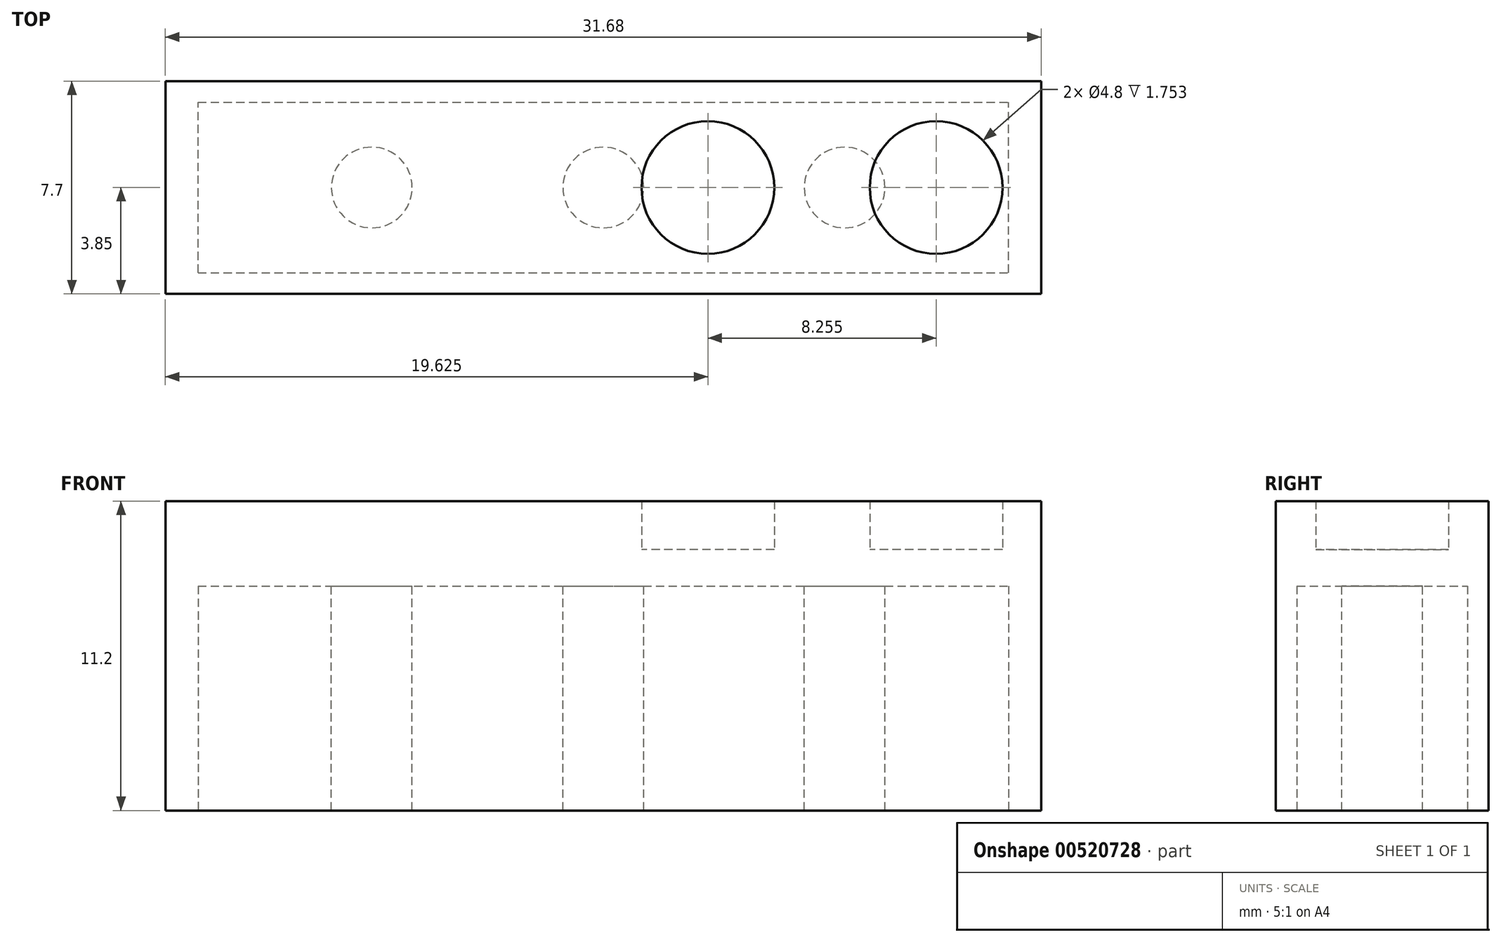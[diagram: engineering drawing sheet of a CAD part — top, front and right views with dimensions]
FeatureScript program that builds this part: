
annotation { "Feature Type Name" : "Feature", "Feature Type Description" : "" }
export const myFeature = defineFeature(function(context is Context, id is Id, definition is map)
    precondition{}
    {
        {
            var Q0;
            Q0=qCreatedBy(makeId("Top.planeOp"),FACE);
            var sketch = newSketch(context, id + "F0", { "sketchPlane" : qUnion([Q0])});
            skLineSegment(sketch, "E0.bottom", {"start": v(-15.84, 3.85) * mm, "end": v(15.84, 3.85) * mm});
            skLineSegment(sketch, "E0.top", {"start": v(-15.84, -3.85) * mm, "end": v(15.84, -3.85) * mm});
            skLineSegment(sketch, "E0.left", {"start": v(-15.84, 3.85) * mm, "end": v(-15.84, -3.85) * mm});
            skLineSegment(sketch, "E0.right", {"start": v(15.84, 3.85) * mm, "end": v(15.84, -3.85) * mm});
            skPoint(sketch, "E0.middle", {"position": v(0, 0) * mm});
            skSolve(sketch);
        }
        {
            var Q0;
            Q0=makeQuery(id+"F0.imprint","IMPRINT",FACE,{"disambiguationData":[TD([[makeQuery(id+"F0.imprint","IMPRINT",EDGE,{"derivedFrom":sQuery(id+"F0.wireOp",EDGE,"E0.bottom")}),-1.0]])]});
            extrude(context, id + "F1", {"entities" : qUnion([Q0]), "depth" : 9.45 * mm, "offsetDistance" : 25.4 * mm});
        }
        {
            var Q0;
            Q0=makeQuery(id+"F1.opExtrude","CAP_FACE",FACE,{"disambiguationData":[OSD([sQuery(id+"F0.wireOp",EDGE,"E0.bottom"),sQuery(id+"F0.wireOp",EDGE,"E0.top"),sQuery(id+"F0.wireOp",EDGE,"E0.left"),sQuery(id+"F0.wireOp",EDGE,"E0.right")])],"isStart":false});
            var sketch = newSketch(context, id + "F2", { "sketchPlane" : qUnion([Q0])});
            skCircle(sketch, "E1", {"center": v(-12.04, 0) * mm, "radius": 2.4 * mm});
            skCircle(sketch, "E2", {"center": v(-3.78, 0) * mm, "radius": 2.4 * mm});
            skCircle(sketch, "E3.MirrorC", {"center": v(3.78, 0) * mm, "radius": 2.4 * mm});
            skCircle(sketch, "E4.MirrorC", {"center": v(12.04, 0) * mm, "radius": 2.4 * mm});
            skSolve(sketch);
        }
        {
            var Q0;
            Q0=makeQuery(id+"F2.imprint","IMPRINT",FACE,{"disambiguationData":[TD([[makeQuery(id+"F2.imprint","IMPRINT",EDGE,{"derivedFrom":sQuery(id+"F2.wireOp",EDGE,"E1")}),1.0]])]});
            var Q1;
            Q1=makeQuery(id+"F2.imprint","IMPRINT",FACE,{"disambiguationData":[TD([[makeQuery(id+"F2.imprint","IMPRINT",EDGE,{"derivedFrom":sQuery(id+"F2.wireOp",EDGE,"E2")}),1.0]])]});
            var Q2;
            Q2=makeQuery(id+"F2.imprint","IMPRINT",FACE,{"disambiguationData":[TD([[makeQuery(id+"F2.imprint","IMPRINT",EDGE,{"derivedFrom":sQuery(id+"F2.wireOp",EDGE,"E3.MirrorC")}),-1.0]])]});
            var Q3;
            Q3=makeQuery(id+"F2.imprint","IMPRINT",FACE,{"disambiguationData":[TD([[makeQuery(id+"F2.imprint","IMPRINT",EDGE,{"derivedFrom":sQuery(id+"F2.wireOp",EDGE,"E4.MirrorC")}),-1.0]])]});
            extrude(context, id + "F3", {"entities" : qUnion([Q0, Q1, Q2, Q3]), "operationType" : NewBodyOperationType.ADD, "depth" : 1.75 * mm, "offsetDistance" : 25.4 * mm});
        }
        {
            var Q0;
            Q0=makeQuery(id+"F1.opExtrude","CAP_FACE",FACE,{"disambiguationData":[OSD([sQuery(id+"F0.wireOp",EDGE,"E0.bottom"),sQuery(id+"F0.wireOp",EDGE,"E0.top"),sQuery(id+"F0.wireOp",EDGE,"E0.left"),sQuery(id+"F0.wireOp",EDGE,"E0.right")])],"isStart":true});
            var sketch = newSketch(context, id + "F4", { "sketchPlane" : qUnion([Q0])});
            skLineSegment(sketch, "E5.bottom", {"start": v(-14.66, 3.09) * mm, "end": v(14.66, 3.09) * mm});
            skLineSegment(sketch, "E5.top", {"start": v(-14.66, -3.09) * mm, "end": v(14.66, -3.09) * mm});
            skLineSegment(sketch, "E5.left", {"start": v(-14.66, 3.09) * mm, "end": v(-14.66, -3.09) * mm});
            skLineSegment(sketch, "E5.right", {"start": v(14.66, 3.09) * mm, "end": v(14.66, -3.09) * mm});
            skPoint(sketch, "E5.middle", {"position": v(0, 0) * mm});
            skSolve(sketch);
        }
        {
            var Q0;
            Q0=makeQuery(id+"F4.imprint","IMPRINT",FACE,{"disambiguationData":[TD([[makeQuery(id+"F4.imprint","IMPRINT",EDGE,{"derivedFrom":sQuery(id+"F4.wireOp",EDGE,"E5.bottom")}),-1.0]])]});
            extrude(context, id + "F5", {"entities" : qUnion([Q0]), "operationType" : NewBodyOperationType.REMOVE, "oppositeDirection" : true, "depth" : 8.13 * mm, "offsetDistance" : 25.4 * mm});
        }
        {
            var Q0;
            Q0=makeQuery(id+"F5.boolean.opBoolean","COPY",FACE,{"derivedFrom":makeQuery(id+"F5.opExtrude","CAP_FACE",FACE,{"disambiguationData":[OSD([sQuery(id+"F4.wireOp",EDGE,"E5.bottom"),sQuery(id+"F4.wireOp",EDGE,"E5.top"),sQuery(id+"F4.wireOp",EDGE,"E5.left"),sQuery(id+"F4.wireOp",EDGE,"E5.right")])],"isStart":false})});
            var sketch = newSketch(context, id + "F6", { "sketchPlane" : qUnion([Q0])});
            skCircle(sketch, "E6", {"center": v(-8.37, 0) * mm, "radius": 1.46 * mm});
            skCircle(sketch, "E7", {"center": v(0, 0) * mm, "radius": 1.46 * mm});
            skCircle(sketch, "E8", {"center": v(8.73, 0) * mm, "radius": 1.46 * mm});
            skSolve(sketch);
        }
        {
            var Q0;
            Q0=makeQuery(id+"F6.imprint","IMPRINT",FACE,{"disambiguationData":[TD([[makeQuery(id+"F6.imprint","IMPRINT",EDGE,{"derivedFrom":sQuery(id+"F6.wireOp",EDGE,"E7")}),1.0]])]});
            var Q1;
            Q1=makeQuery(id+"F6.imprint","IMPRINT",FACE,{"disambiguationData":[TD([[makeQuery(id+"F6.imprint","IMPRINT",EDGE,{"derivedFrom":sQuery(id+"F6.wireOp",EDGE,"E8")}),1.0]])]});
            var Q2;
            Q2=makeQuery(id+"F6.imprint","IMPRINT",FACE,{"disambiguationData":[TD([[makeQuery(id+"F6.imprint","IMPRINT",EDGE,{"derivedFrom":sQuery(id+"F6.wireOp",EDGE,"E6")}),1.0]])]});
            extrude(context, id + "F7", {"entities" : qUnion([Q0, Q1, Q2]), "operationType" : NewBodyOperationType.ADD, "depth" : 8.13 * mm, "offsetDistance" : 25.4 * mm});
        }
    });
